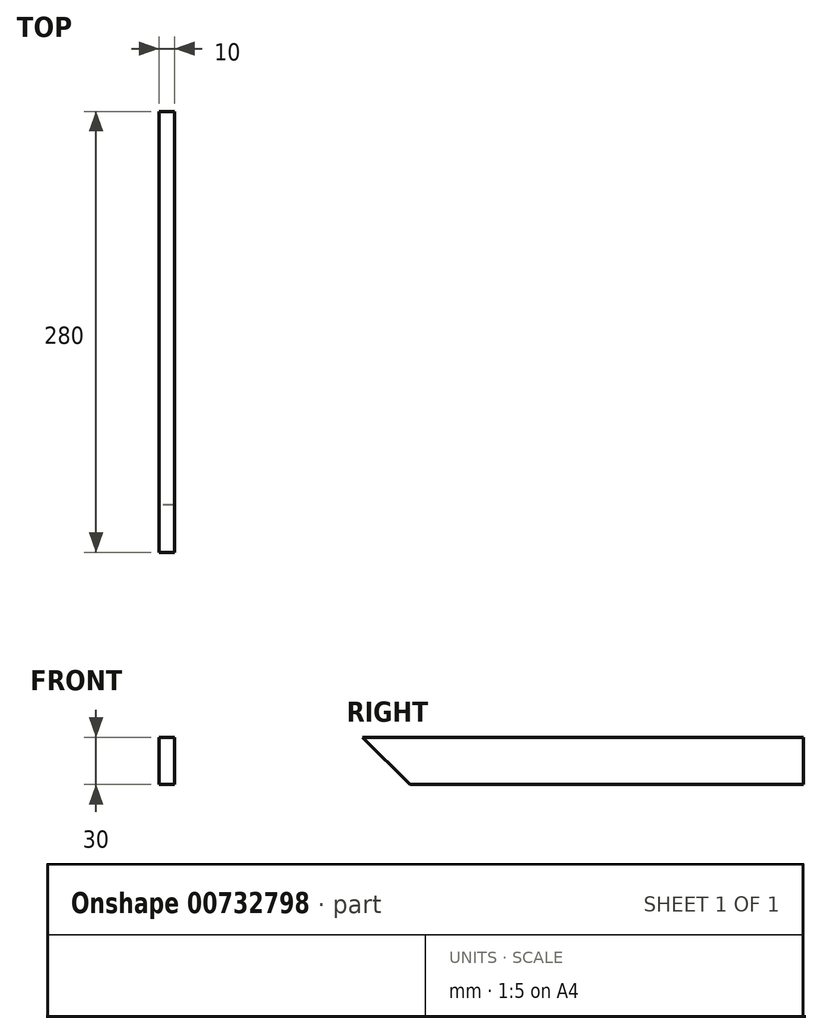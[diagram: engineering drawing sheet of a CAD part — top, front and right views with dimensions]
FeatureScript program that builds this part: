
annotation { "Feature Type Name" : "Feature", "Feature Type Description" : "" }
export const myFeature = defineFeature(function(context is Context, id is Id, definition is map)
    precondition{}
    {
        {
            var Q0;
            Q0=qCreatedBy(makeId("Right.planeOp"),FACE);
            var sketch = newSketch(context, id + "F0", { "sketchPlane" : qUnion([Q0])});
            skLineSegment(sketch, "E0", {"start": v(-100, -15) * mm, "end": v(150, -15) * mm});
            skLineSegment(sketch, "E1", {"start": v(150, 15) * mm, "end": v(-130, 15) * mm});
            skLineSegment(sketch, "E2", {"start": v(-130, 15) * mm, "end": v(-100, -15) * mm});
            skLineSegment(sketch, "E3", {"start": v(-100, -15) * mm, "end": v(-100, 15) * mm, "construction": true});
            skLineSegment(sketch, "E4", {"start": v(150, -15) * mm, "end": v(150, 15) * mm});
            skSolve(sketch);
        }
        {
            var Q0;
            Q0 = qSketchRegion(id + "F0", true);
            extrude(context, id + "F1", {"entities" : qUnion([Q0]), "depth" : 10 * mm, "offsetDistance" : 25 * mm});
        }
    });
